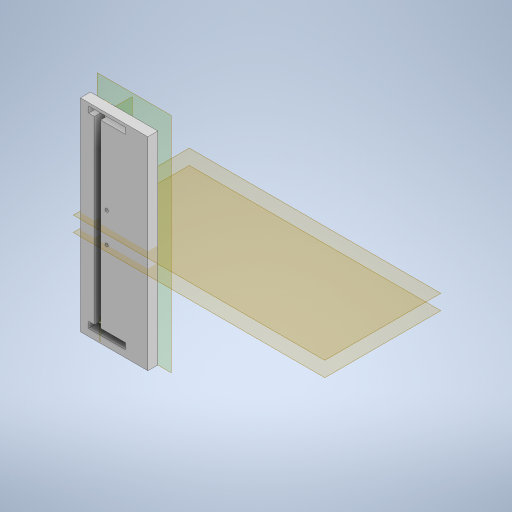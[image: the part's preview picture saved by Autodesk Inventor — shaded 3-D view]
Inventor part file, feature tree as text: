
AUTODESK INVENTOR PART (.ipt)
format: ipt  version: 2024.2 (Build 282272000, 272)  size: 325,120 bytes
history: native  units: mm
features: other x11, sketch x6, extrude x6, projected_geometry x3, mirror x2
ambient origin geometry x8: Origin, YZ Plane, XZ Plane, XY Plane, X Axis, Y Axis, Z Axis, Center Point
bodies: Body1 (feature_tree)
feature tree (28):
  other  "Твердое тело1"
  other  "РабПлоскость1"
  sketch  "Эскиз1"
  other  "РабПлоскость2"
  extrude  "Выдавливание2"  Depth=3.0mm
  other  "РабПлоскость3"
  mirror  "Зеркальное отражение1"
  other  "РабПлоскость7"
  extrude  "Выдавливание3"  Depth=3.0mm
  other  "РабПлоскость4"
  extrude  "Выдавливание4"  Depth=6.0mm
  mirror  "Зеркальное отражение2"
  other  "РабПлоскость6"
  extrude  "Выдавливание5"  Depth=6.0mm
  other  "РабПлоскость5"
  extrude  "Выдавливание6"  Depth=15.0mm
  extrude  "Выдавливание7"  Depth=15.0mm
  sketch  "Эскиз2"
  sketch  "Эскиз3"
  projected_geometry  "Спроецированная петля1"
  sketch  "Эскиз4"
  projected_geometry  "Спроецированная петля2"
  sketch  "Эскиз5"
  sketch  "Эскиз6"
  projected_geometry  "Спроецированная петля3"
  other  "<userpath>\Documents\Artist\3D\Робот.iam"
  other  "Робот.iam"
  other  "передняя стенка:1"
